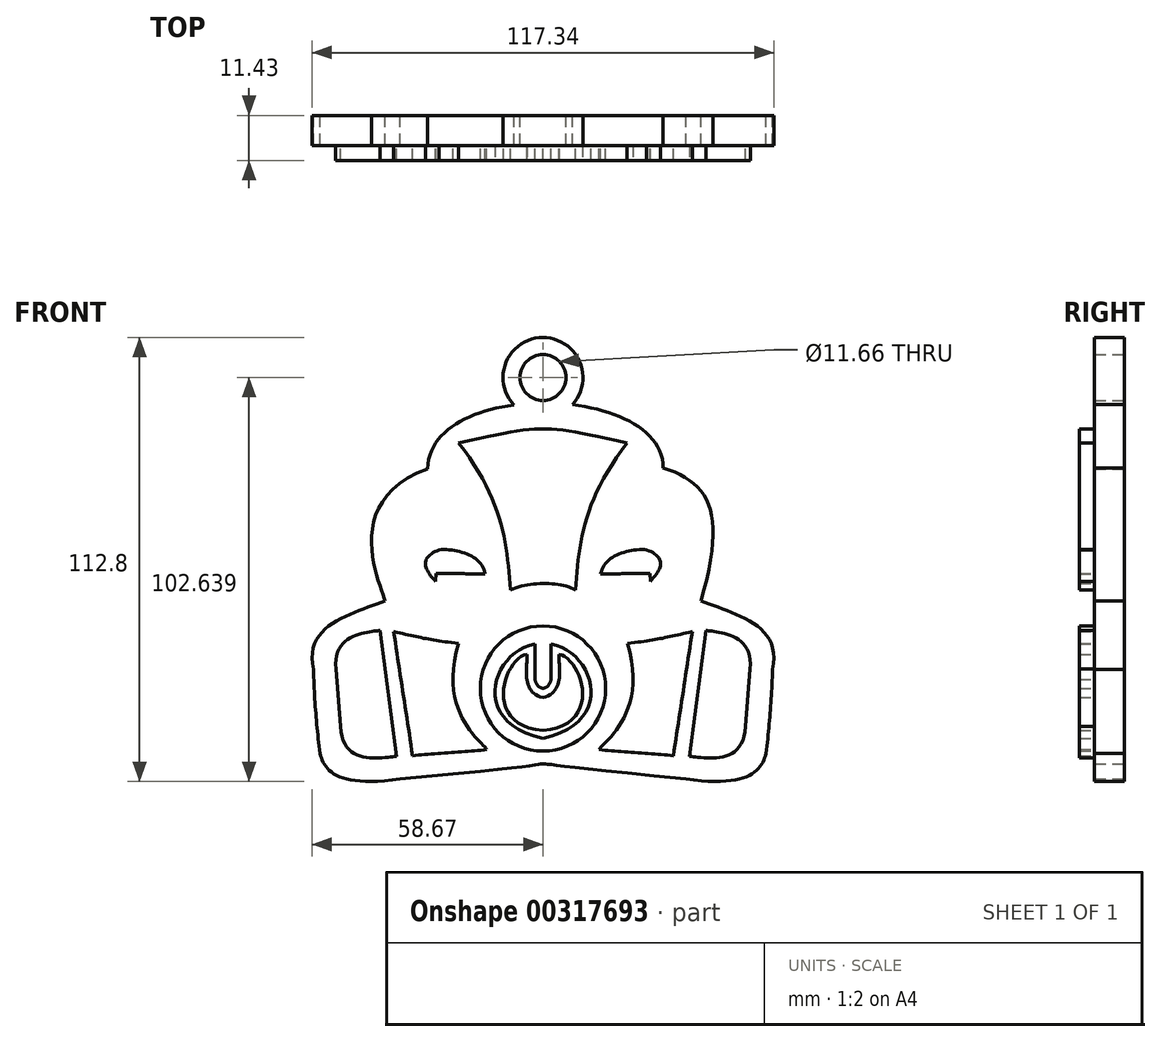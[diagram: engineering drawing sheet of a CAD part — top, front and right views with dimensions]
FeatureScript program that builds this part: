
annotation { "Feature Type Name" : "Feature", "Feature Type Description" : "" }
export const myFeature = defineFeature(function(context is Context, id is Id, definition is map)
    precondition{}
    {
        {
            var Q0;
            Q0=qCreatedBy(makeId("Front.planeOp"),FACE);
            var sketch = newSketch(context, id + "F0", { "sketchPlane" : qUnion([Q0])});
            skFitSpline(sketch, "E0", {"points": [v(-40.16, -4.93) * mm, v(-29.28, 28.6) * mm], "startDerivative": vector(-4.08, 14.8) * mm, "endDerivative": vector(66.61, 24.47) * mm});
            skFitSpline(sketch, "E1", {"points": [v(-29.28, 28.6) * mm, v(30.53, 28.82) * mm], "startDerivative": vector(1.44, 68.84) * mm, "endDerivative": vector(-0.6, -63.84) * mm});
            skFitSpline(sketch, "E2", {"points": [v(30.53, 28.82) * mm, v(40.16, -4.93) * mm], "startDerivative": vector(36.03, -11.56) * mm, "endDerivative": vector(-19.45, -66.97) * mm});
            skFitSpline(sketch, "E3", {"points": [v(-40.16, -4.93) * mm, v(-58.33, -22.39) * mm], "startDerivative": vector(-21.75, -9.52) * mm, "endDerivative": vector(7.92, -36) * mm});
            skFitSpline(sketch, "E4", {"points": [v(-56.66, -43.75) * mm, v(-58.33, -22.39) * mm], "startDerivative": vector(-2.72, 21.98) * mm, "endDerivative": vector(-0.72, 22.32) * mm});
            skFitSpline(sketch, "E5", {"points": [v(-56.66, -43.75) * mm, v(-36.3, -50.25) * mm], "startDerivative": vector(3.4, -12.91) * mm, "endDerivative": vector(48.26, 6.8) * mm});
            skFitSpline(sketch, "E6.MirrorCS", {"points": [v(56.66, -43.75) * mm, v(58.33, -22.39) * mm], "startDerivative": vector(2.72, 21.98) * mm, "endDerivative": vector(0.72, 22.32) * mm});
            skFitSpline(sketch, "E7.MirrorCS", {"points": [v(40.16, -4.93) * mm, v(58.33, -22.39) * mm], "startDerivative": vector(21.75, -9.52) * mm, "endDerivative": vector(-7.92, -36) * mm});
            skFitSpline(sketch, "E8.MirrorCS", {"points": [v(56.66, -43.75) * mm, v(36.3, -50.25) * mm], "startDerivative": vector(-3.4, -12.91) * mm, "endDerivative": vector(-48.26, 6.8) * mm});
            skFitSpline(sketch, "E9", {"points": [v(-36.3, -50.25) * mm, v(0, -46.4) * mm, v(36.3, -50.25) * mm], "startDerivative": vector(202.74, 18.7) * mm, "endDerivative": vector(201.98, -20.2) * mm});
            skSolve(sketch);
        }
        {
            var Q0;
            Q0 = qSketchRegion(id + "F0", true);
            extrude(context, id + "F1", {"entities" : qUnion([Q0]), "depth" : 7.62 * mm});
        }
        {
            var Q0;
            Q0=makeQuery(id+"F1.opExtrude","CAP_FACE",FACE,{"disambiguationData":[OSD([sQuery(id+"F0.wireOp",EDGE,"E0"),sQuery(id+"F0.wireOp",EDGE,"E1"),sQuery(id+"F0.wireOp",EDGE,"E2"),sQuery(id+"F0.wireOp",EDGE,"E3"),sQuery(id+"F0.wireOp",EDGE,"E4"),sQuery(id+"F0.wireOp",EDGE,"E5"),sQuery(id+"F0.wireOp",EDGE,"E6.MirrorCS"),sQuery(id+"F0.wireOp",EDGE,"E7.MirrorCS"),sQuery(id+"F0.wireOp",EDGE,"E8.MirrorCS"),sQuery(id+"F0.wireOp",EDGE,"E9")])],"isStart":false});
            var sketch = newSketch(context, id + "F2", { "sketchPlane" : qUnion([Q0])});
            skFitSpline(sketch, "E10", {"points": [v(-8.3, -2.17) * mm, v(-21.4, 35.12) * mm], "startDerivative": vector(-2.34, 34.98) * mm, "endDerivative": vector(-33.95, 43.65) * mm});
            skFitSpline(sketch, "E11.MirrorCS", {"points": [v(8.3, -2.17) * mm, v(21.4, 35.12) * mm], "startDerivative": vector(2.34, 34.98) * mm, "endDerivative": vector(33.95, 43.65) * mm});
            skFitSpline(sketch, "E12", {"points": [v(-21.4, 35.12) * mm, v(21.4, 35.12) * mm], "startDerivative": vector(64.2, 14.53) * mm, "endDerivative": vector(64.2, -14.53) * mm});
            skFitSpline(sketch, "E13", {"points": [v(-8.3, -2.17) * mm, v(8.3, -2.17) * mm], "startDerivative": vector(15.24, 6.52) * mm, "endDerivative": vector(12.2, -6.52) * mm});
            skFitSpline(sketch, "E14", {"points": [v(-37.93, -12.75) * mm, v(-33.13, -44.31) * mm], "startDerivative": vector(4.8, -31.93) * mm, "endDerivative": vector(4.8, -31.93) * mm});
            skFitSpline(sketch, "E15", {"points": [v(-33.13, -44.31) * mm, v(-14.28, -42.75) * mm], "startDerivative": vector(16.8, 1.92) * mm, "endDerivative": vector(16.8, 1.92) * mm});
            skFitSpline(sketch, "E16", {"points": [v(-37.93, -12.75) * mm, v(-21.48, -15.75) * mm], "startDerivative": vector(18.72, -4.32) * mm, "endDerivative": vector(21.6, -2.16) * mm});
            skFitSpline(sketch, "E17", {"points": [v(-14.28, -42.75) * mm, v(-21.48, -15.75) * mm], "startDerivative": vector(-3.24, 6.12) * mm, "endDerivative": vector(15.84, 54.01) * mm});
            skFitSpline(sketch, "E18.MirrorCS", {"points": [v(37.93, -12.75) * mm, v(33.13, -44.31) * mm], "startDerivative": vector(-4.8, -31.93) * mm, "endDerivative": vector(-4.8, -31.93) * mm});
            skFitSpline(sketch, "E19.MirrorCS", {"points": [v(37.93, -12.75) * mm, v(21.48, -15.75) * mm], "startDerivative": vector(-18.72, -4.32) * mm, "endDerivative": vector(-21.6, -2.16) * mm});
            skFitSpline(sketch, "E20.MirrorCS", {"points": [v(14.28, -42.75) * mm, v(21.48, -15.75) * mm], "startDerivative": vector(3.24, 6.12) * mm, "endDerivative": vector(-15.84, 54.01) * mm});
            skFitSpline(sketch, "E21.MirrorCS", {"points": [v(33.13, -44.31) * mm, v(14.28, -42.75) * mm], "startDerivative": vector(-16.8, 1.92) * mm, "endDerivative": vector(-16.8, 1.92) * mm});
            skCircle(sketch, "E22", {"center": v(0, -27.23) * mm, "radius": 15.9 * mm});
            skFitSpline(sketch, "E23", {"points": [v(-2.08, -15.9) * mm, v(0, -39.95) * mm], "startDerivative": vector(-32.37, -5.93) * mm, "endDerivative": vector(56.75, -12.7) * mm});
            skFitSpline(sketch, "E24.MirrorCS", {"points": [v(2.08, -15.9) * mm, v(0, -39.95) * mm], "startDerivative": vector(32.37, -5.93) * mm, "endDerivative": vector(-56.75, -12.7) * mm});
            skFitSpline(sketch, "E25", {"points": [v(-27.26, 0) * mm, v(-26.36, 8) * mm], "startDerivative": vector(-11.06, 11.33) * mm, "endDerivative": vector(13.49, 5.4) * mm});
            skFitSpline(sketch, "E26", {"points": [v(-26.36, 8) * mm, v(-14.67, 1.89) * mm], "startDerivative": vector(14.03, 1.08) * mm, "endDerivative": vector(2.43, -14.03) * mm});
            skFitSpline(sketch, "E27", {"points": [v(-27.17, 1.98) * mm, v(-14.67, 1.89) * mm], "startDerivative": vector(11.42, -0.18) * mm, "endDerivative": vector(11.42, -0.18) * mm});
            skFitSpline(sketch, "E28", {"points": [v(-27.26, 0) * mm, v(-27.17, 1.98) * mm], "startDerivative": vector(0.09, 1.98) * mm, "endDerivative": vector(0.09, 1.98) * mm});
            skFitSpline(sketch, "E29.MirrorCS", {"points": [v(27.17, 1.98) * mm, v(14.67, 1.89) * mm], "startDerivative": vector(-11.42, -0.18) * mm, "endDerivative": vector(-11.42, -0.18) * mm});
            skFitSpline(sketch, "E30.MirrorCS", {"points": [v(27.26, 0) * mm, v(26.36, 8) * mm], "startDerivative": vector(11.06, 11.33) * mm, "endDerivative": vector(-13.49, 5.4) * mm});
            skFitSpline(sketch, "E31.MirrorCS", {"points": [v(26.36, 8) * mm, v(14.67, 1.89) * mm], "startDerivative": vector(-14.03, 1.08) * mm, "endDerivative": vector(-2.43, -14.03) * mm});
            skFitSpline(sketch, "E32.MirrorCS", {"points": [v(27.26, 0) * mm, v(27.17, 1.98) * mm], "startDerivative": vector(-0.09, 1.98) * mm, "endDerivative": vector(-0.09, 1.98) * mm});
            skFitSpline(sketch, "E33", {"points": [v(-4.05, -18.57) * mm, v(0, -37.94) * mm], "startDerivative": vector(-17, -2.38) * mm, "endDerivative": vector(47.17, -4.42) * mm});
            skFitSpline(sketch, "E34", {"points": [v(-4.05, -18.57) * mm, v(0, -29.56) * mm], "startDerivative": vector(0.34, -9.86) * mm, "endDerivative": vector(16.92, -4.08) * mm});
            skFitSpline(sketch, "E35.MirrorCS", {"points": [v(4.05, -18.57) * mm, v(0, -37.94) * mm], "startDerivative": vector(17, -2.38) * mm, "endDerivative": vector(-47.17, -4.42) * mm});
            skFitSpline(sketch, "E36.MirrorCS", {"points": [v(4.05, -18.57) * mm, v(0, -29.56) * mm], "startDerivative": vector(-0.34, -9.86) * mm, "endDerivative": vector(-16.92, -4.08) * mm});
            skFitSpline(sketch, "E37", {"points": [v(-41.44, -12.42) * mm, v(-37.27, -44.47) * mm], "startDerivative": vector(4.18, -32.06) * mm, "endDerivative": vector(4.18, -32.06) * mm});
            skFitSpline(sketch, "E38", {"points": [v(-41.44, -12.42) * mm, v(-52.62, -22.24) * mm], "startDerivative": vector(-4.45, -1.62) * mm, "endDerivative": vector(2.73, -29.44) * mm});
            skFitSpline(sketch, "E39", {"points": [v(-37.27, -44.47) * mm, v(-51.41, -36.92) * mm], "startDerivative": vector(-8.9, -0.4) * mm, "endDerivative": vector(-1.27, 31.67) * mm});
            skFitSpline(sketch, "E40", {"points": [v(-52.62, -22.24) * mm, v(-51.41, -36.92) * mm], "startDerivative": vector(1.21, -14.68) * mm, "endDerivative": vector(1.21, -14.68) * mm});
            skFitSpline(sketch, "E41", {"points": [v(-2.08, -15.9) * mm, v(-2.08, -24.94) * mm], "startDerivative": vector(0, -8.43) * mm, "endDerivative": vector(0, -8.43) * mm});
            skFitSpline(sketch, "E42", {"points": [v(0, -27.23) * mm, v(-2.08, -24.94) * mm], "startDerivative": vector(-3.28, 1.03) * mm, "endDerivative": vector(-1.66, 5) * mm});
            skFitSpline(sketch, "E43.MirrorCS", {"points": [v(37.27, -44.47) * mm, v(51.41, -36.92) * mm], "startDerivative": vector(8.9, -0.4) * mm, "endDerivative": vector(1.27, 31.67) * mm});
            skFitSpline(sketch, "E44.MirrorCS", {"points": [v(52.62, -22.24) * mm, v(51.41, -36.92) * mm], "startDerivative": vector(-1.21, -14.68) * mm, "endDerivative": vector(-1.21, -14.68) * mm});
            skFitSpline(sketch, "E45.MirrorCS", {"points": [v(41.44, -12.42) * mm, v(52.62, -22.24) * mm], "startDerivative": vector(4.45, -1.62) * mm, "endDerivative": vector(-2.73, -29.44) * mm});
            skFitSpline(sketch, "E46.MirrorCS", {"points": [v(41.44, -12.42) * mm, v(37.27, -44.47) * mm], "startDerivative": vector(-4.18, -32.06) * mm, "endDerivative": vector(-4.18, -32.06) * mm});
            skFitSpline(sketch, "E47.MirrorCS", {"points": [v(2.08, -15.9) * mm, v(2.08, -24.94) * mm], "startDerivative": vector(0, -8.43) * mm, "endDerivative": vector(0, -8.43) * mm});
            skFitSpline(sketch, "E48.MirrorCS", {"points": [v(0, -27.23) * mm, v(2.08, -24.94) * mm], "startDerivative": vector(3.28, 1.03) * mm, "endDerivative": vector(1.66, 5) * mm});
            skSolve(sketch);
        }
        {
            var Q0;
            Q0 = qSketchRegion(id + "F2", true);
            var Q1;
            Q1=makeQuery(id+"F2.imprint","IMPRINT",FACE,{"disambiguationData":[TD([[makeQuery(id+"F2.imprint","IMPRINT",EDGE,{"derivedFrom":sQuery(id+"F2.wireOp",EDGE,"E33")}),1.0]])]});
            extrude(context, id + "F3", {"entities" : qUnion([Q0, Q1]), "operationType" : NewBodyOperationType.ADD, "depth" : 3.8 * mm});
        }
        {
            var Q0;
            Q0=qCreatedBy(makeId("Front.planeOp"),FACE);
            var sketch = newSketch(context, id + "F4", { "sketchPlane" : qUnion([Q0])});
            skCircle(sketch, "E49", {"center": v(0, 51.78) * mm, "radius": 10.16 * mm});
            skCircle(sketch, "E50", {"center": v(0, 51.78) * mm, "radius": 5.83 * mm});
            skSolve(sketch);
        }
        {
            var Q0;
            Q0 = qSketchRegion(id + "F4", true);
            extrude(context, id + "F5", {"entities" : qUnion([Q0]), "operationType" : NewBodyOperationType.ADD, "depth" : 7.62 * mm});
        }
    });
